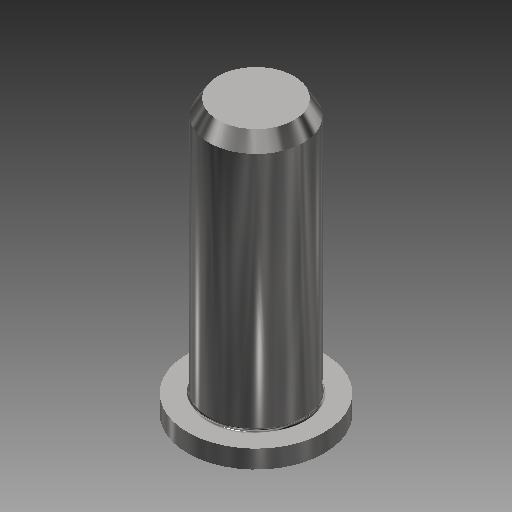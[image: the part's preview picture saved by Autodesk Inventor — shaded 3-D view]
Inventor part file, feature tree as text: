
AUTODESK INVENTOR PART (.ipt)
format: ipt  version: 2019 (Build 230136000, 136)  size: 140,800 bytes
history: native  units: in
note: dims shown in document units (in); Inventor stores cm internally (conversion verified against a paired STEP export)
features: extrude x2, sketch x2, plane x1, fillet x1, chamfer x1
ambient origin geometry x8: Origin, YZ Plane, XZ Plane, XY Plane, X Axis, Y Axis, Z Axis, Center Point
bodies: Solid1 (feature_tree)
feature tree (7):
  plane  "Work Plane2"
  extrude  "Extrusion1"  Depth=0.252in
  extrude  "Extrusion2"  Depth=0.0098in
  fillet  "Fillet1"  Radius=0.8425in
  chamfer  "Chamfer2"  Distance=0.311in
  sketch  "Sketch1"  dims[d1=19.4699in d2=0.252in]
  sketch  "Sketch2"  dims[d3=16.2375in d4=120.8203in d5=0.8425in d6=0.0in d7=0.311in d8=0.45in d9=0.0598in d10=0.0in d11=0.0098in d15=0.05in d16=0.0297in d17=45.0deg]
